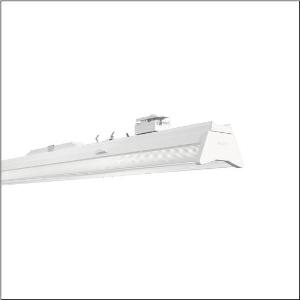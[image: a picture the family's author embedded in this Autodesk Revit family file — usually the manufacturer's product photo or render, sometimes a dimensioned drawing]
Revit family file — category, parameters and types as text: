
# Revit family: licross_r__21_performance_mo_52td16dn4a5g_459a
name_source: partatom
category: Lighting Fixtures
units: mm (PartAtom-declared; Revit-internal decimal feet)

## family parameters
Cut with Voids When Loaded = No
Host = Face
Light Source = No
Part Type = Normal
Room Calculation Point = No
Round Connector Dimension = Use Diameter
Shared = No

## types (1)
- --- (1 x LED, 10840 lm, 62 W, 4000K)
    Apparent Load = 62 VA
    CIE Flux Codes = 66 88 96 79 100
    Color Rendering = 80
    Color Temperature = 4000K
    Default Elevation = 1800 mm
    Description = Licross® 21 Performance MO, luminaire insert, of sheet steel, galvanised, coil coated, white, length: 1.500mm, width: 120mm, height: 123mm, LED rated luminous flux: 10.840lm, light colour: 840, SDCM (Standard Deviation of Colour Matching)MacAdam ≤ 3 SDCM (initial), control gear: DALI 2, with plug, 5-pole, with phase selection, mains connection: 220..240V, AC, 50/60Hz, rated input power: 62W, internal wiring halogen-free, primary light control with lens, of plastic, primary optical cover: cover, of PMMA, light emission: direct/indirect distribution, primary light characteristic: symmetric, protection rating (complete): IP54, insulation class (complete): insulation class I (protective earthing), certification: CE, ENEC, VDE, UKCA, protection symbol: D if used in an environment with non-conductive dust loads with corresponding accessories, impact resistance: IK06, permissible ambient temperature for indoor applications: -25..+35°C, corresponds to IFS (International Featured Standards) requirements for safety and quality in the food industry, reducing of maximum allowable ambient temperature of 5°C with ceiling mounting, LABS conformity tested according to VDMA 24364:2018-05, packaging unit: 1 piece
    Height = 114 mm
    Lamp = 1 x LED
    Lamp Light Flux = 10840 lm
    Lamp Power = 62 W
    Lamp count = 1
    Length = 1500 mm
    Luminous efficacy = 175 lm/W
    Manufacturer = Siteco
    ModVariant = No
    Model = 52TD16DN4A5G
    Mounting Place = Ceiling
    Mounting Type = Pendant
    Number of Poles = 1
    OnlyDefault = Yes
    Power Factor = 1
    Product Name = Licross® 21 Performance MO
    Product group = luminaire insert | ceiling pendant
    ProductGroupID = 901
    Protection Class = Protection class I
    Protection Degree = IP 54
    RLX_Detail_Level = 1
    RLX_Emergency_Light_Flux = 0 lm
    RLX_Emergency_Type = 0
    RLX_Emergency_Type_DB = No
    RlxData = <blob elided: 34205 chars, md5=8d69f610>
    Socket = socket
    Standby Power = 0 W
    System Light Flux = 10840 lm
    System Power = 62 W
    Type Comments = factory setting: luminous flux: 100 % | dim-lin: 254 | 418 mA
    Type Image = l_1256138.jpg
    URL = http://relux.com
    VarID = @adj_133095
    Voltage = 0 V
    Weight = 0.00 kg
    Width = 120 mm

## geometry (parser evidence)
native form markers: Blend x4, Sweep x12
no freeform markers — native parametric forms only
